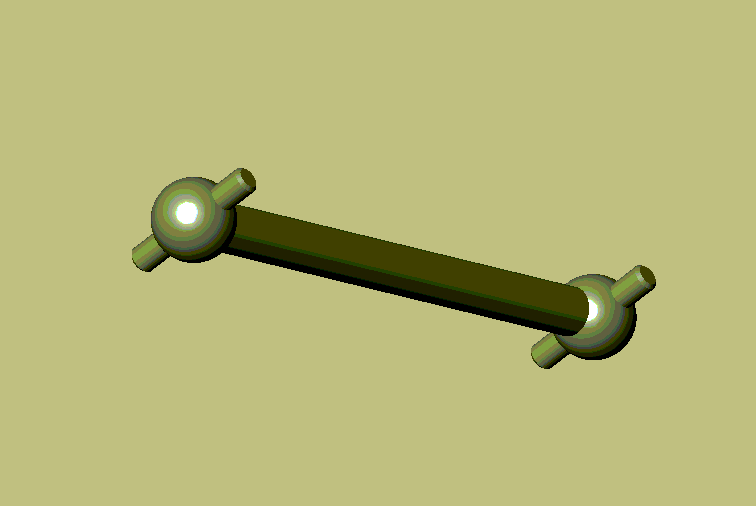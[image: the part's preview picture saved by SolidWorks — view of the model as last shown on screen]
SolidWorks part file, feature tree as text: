
SOLIDWORKS PART (.sldprt)
format: sldprt  version: not decoded by parser v0  size: 159,744 bytes
history: native  units: mm
features: plane x3, sketch x3, material x1, revolve x1, extrude x1, chamfer x1 + 1 further entry (+7 scaffold rows collapsed)
feature tree (18):
  scaffold x7  (default folders/planes/origin — collapsed)
  material  "Matériau <non spécifié>"
  "Corps de surface"
  plane  "Plane1"
  plane  "Plane2"
  plane  "Plane3"
  sketch  "Esquisse1"  dims[D1=6.0mm D2=6.0mm D3=42.0mm D4=1.75mm]
  revolve  "Base-Révolution"  Angle=360deg
  sketch  "Esquisse3"  dims[D1=2.0mm D2=2.0mm D3=42.0mm]
  extrude  "Boss.-Extru.1"  Depth=11mm
  chamfer  "Chanfrein1"  Distance=0.25mm Angle=45deg
  sketch  "Esquisse4"
decode coverage: 5 of 6 modeling features carry decoded parameters; 1 rows unclassified (native names shown)
note: suppression state not decoded; provenance and decode notes live in map.json
